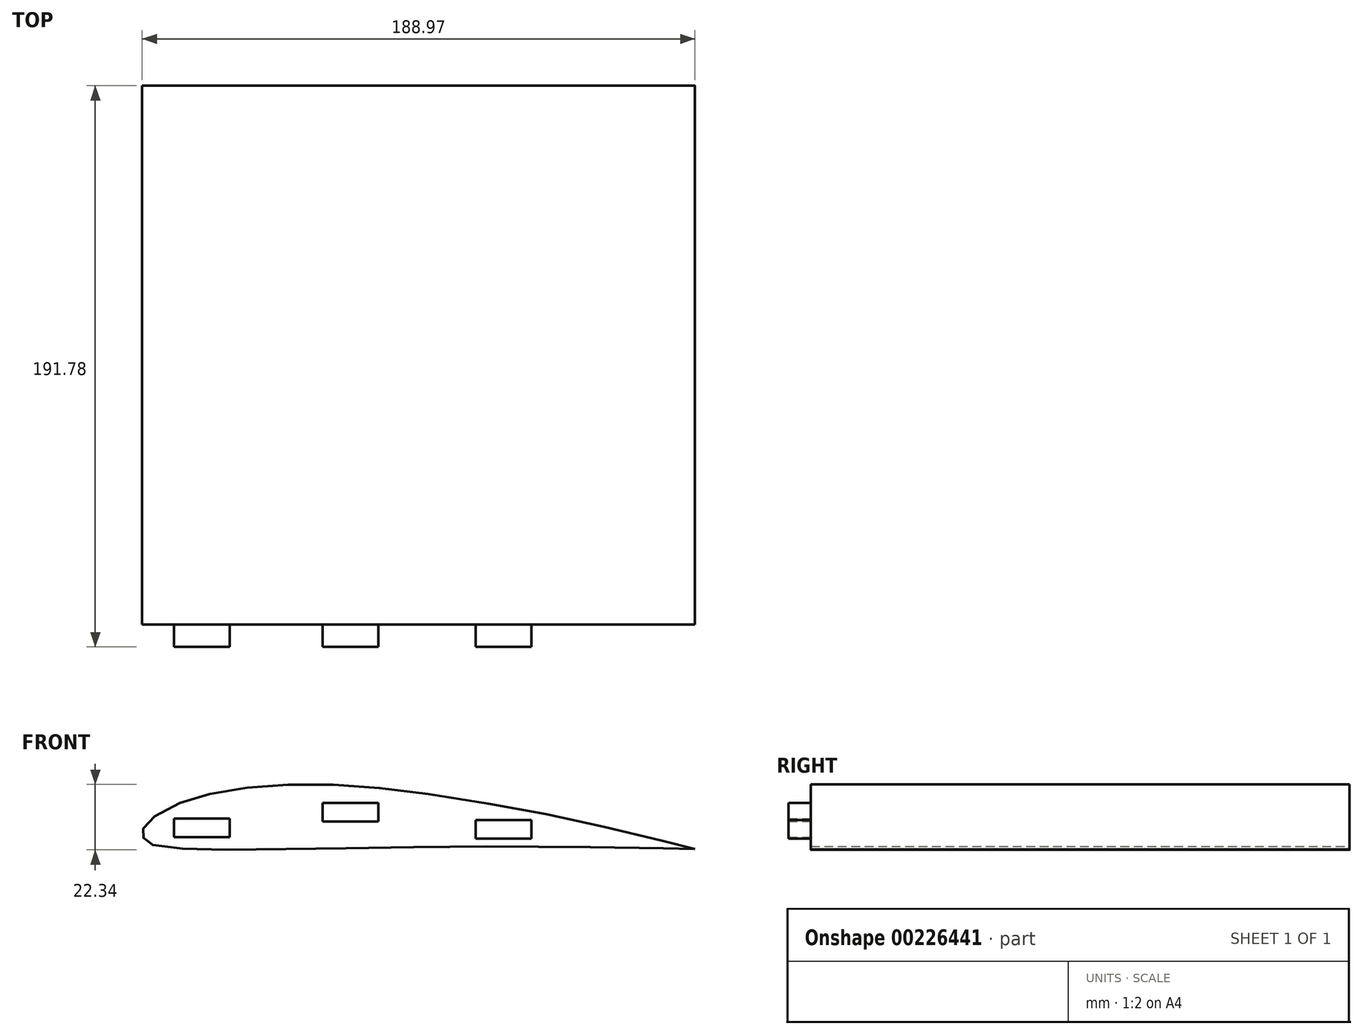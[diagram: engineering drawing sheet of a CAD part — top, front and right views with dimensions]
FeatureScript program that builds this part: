
annotation { "Feature Type Name" : "Feature", "Feature Type Description" : "" }
export const myFeature = defineFeature(function(context is Context, id is Id, definition is map)
    precondition{}
    {
        {
            var Q0;
            Q0=qCreatedBy(makeId("Front.planeOp"),FACE);
            var sketch = newSketch(context, id + "F0", { "sketchPlane" : qUnion([Q0])});
            skFitSpline(sketch, "E0.0", {"points": [v(330.51, -26.8) * mm, v(330.41, -27.02) * mm, v(320.9, -26.65) * mm, v(282.9, -25.74) * mm, v(133.46, -23.45) * mm, v(-1.4, -24.3) * mm, v(-5.52, -24.35) * mm, v(-223.27, -27.63) * mm, v(-263.84, -26.15) * mm, v(-289.63, -25.37) * mm, v(-306.1, -22.64) * mm, v(-310.34, -21.37) * mm, v(-312.97, -20.17) * mm, v(-315.36, -18.5) * mm, v(-317.44, -16.46) * mm, v(-318.92, -14.43) * mm, v(-319.94, -12.57) * mm, v(-320.57, -10.76) * mm, v(-320.82, -9.61) * mm, v(-320.99, -7.97) * mm, v(-320.86, -6.28) * mm, v(-320.4, -4.3) * mm, v(-319.53, -2.04) * mm, v(-317.5, 1.34) * mm, v(-314.64, 4.78) * mm, v(-309.38, 9.62) * mm, v(-300.92, 15.27) * mm, v(-284.86, 23.88) * mm, v(-268.85, 30.71) * mm, v(-251.3, 35.74) * mm, v(-225.1, 41.46) * mm, v(-196.52, 45.77) * mm, v(-164.68, 48.46) * mm, v(-128.36, 49.34) * mm, v(-84.95, 48.6) * mm, v(-42.8, 45.45) * mm, v(0.59, 40.3) * mm, v(69.38, 29.76) * mm, v(139.47, 17.63) * mm, v(201.78, 4.38) * mm, v(277.63, -13.26) * mm, v(320.71, -24.55) * mm, v(330.61, -26.58) * mm, v(330.51, -26.8) * mm]});
            skPoint(sketch, "E1", {"position": v(330.51, -26.8) * mm});
            skPoint(sketch, "E2", {"position": v(-320.85, -9.19) * mm});
            skSolve(sketch);
        }
        {
            var Q0;
            Q0=makeQuery(id+"F0.imprint","IMPRINT",FACE,{"disambiguationData":[TD([[makeQuery(id+"F0.imprint","IMPRINT",EDGE,{"derivedFrom":sQuery(id+"F0.wireOp",EDGE,"E0.0")}),-1.0]])]});
            extrude(context, id + "F1", {"entities" : qUnion([Q0]), "depth" : 635 * mm, "symmetric" : true});
        }
        {
            var Q0;
            Q0=makeQuery(id+"F1.opExtrude","SWEPT_BODY",BODY,{"disambiguationData":[OSD([sQuery(id+"F0.wireOp",EDGE,"E0.0")])]});
            var Q1;
            Q1=qCreatedBy(makeId("Origin.pointOp"),VERTEX);
            transform(context, id + "F2", {"entities" : qUnion([Q0]), "transformType" : TransformType.SCALE_UNIFORMLY, "scale" : .29, "scalePoint" : qUnion([Q1]), "makeCopy" : false});
        }
        {
            var Q0;
            Q0=makeQuery(id+"F1.opExtrude","CAP_FACE",FACE,{"disambiguationData":[OSD([sQuery(id+"F0.wireOp",EDGE,"E0.0")])],"isStart":false});
            var sketch = newSketch(context, id + "F3", { "sketchPlane" : qUnion([Q0])});
            skFitSpline(sketch, "E3.0", {"points": [v(95.85, -7.77) * mm, v(95.82, -7.84) * mm, v(93.06, -7.73) * mm, v(82.04, -7.47) * mm, v(38.7, -6.8) * mm, v(-0.4, -7.05) * mm, v(-1.6, -7.06) * mm, v(-64.75, -8.01) * mm, v(-76.51, -7.58) * mm, v(-84, -7.36) * mm, v(-88.77, -6.57) * mm, v(-90, -6.2) * mm, v(-90.76, -5.85) * mm, v(-91.45, -5.37) * mm, v(-92.06, -4.77) * mm, v(-92.49, -4.19) * mm, v(-92.78, -3.65) * mm, v(-92.96, -3.12) * mm, v(-93.04, -2.79) * mm, v(-93.09, -2.31) * mm, v(-93.05, -1.82) * mm, v(-92.92, -1.25) * mm, v(-92.66, -0.6) * mm, v(-92.08, 0.39) * mm, v(-91.24, 1.39) * mm, v(-89.72, 2.79) * mm, v(-87.27, 4.43) * mm, v(-82.61, 6.93) * mm, v(-77.97, 8.9) * mm, v(-72.88, 10.37) * mm, v(-65.28, 12.02) * mm, v(-57, 13.27) * mm, v(-47.76, 14.05) * mm, v(-37.23, 14.3) * mm, v(-24.64, 14.1) * mm, v(-12.41, 13.18) * mm, v(0.17, 11.69) * mm, v(20.12, 8.63) * mm, v(40.45, 5.11) * mm, v(58.52, 1.27) * mm, v(80.51, -3.84) * mm, v(93, -7.12) * mm, v(95.88, -7.7) * mm, v(95.85, -7.77) * mm]});
            skPoint(sketch, "E4", {"position": v(-93.07, -2.2) * mm});
            skPoint(sketch, "E5", {"position": v(95.64, -7.8) * mm});
            skLineSegment(sketch, "E6.bottom", {"start": v(-63.23, -3.61) * mm, "end": v(-82.28, -3.61) * mm});
            skLineSegment(sketch, "E6.top", {"start": v(-63.23, 2.74) * mm, "end": v(-82.28, 2.74) * mm});
            skLineSegment(sketch, "E6.left", {"start": v(-63.23, -3.61) * mm, "end": v(-63.23, 2.74) * mm});
            skLineSegment(sketch, "E6.right", {"start": v(-82.28, -3.61) * mm, "end": v(-82.28, 2.74) * mm});
            skPoint(sketch, "E6.middle", {"position": v(-72.75, -0.44) * mm});
            skLineSegment(sketch, "E7.bottom", {"start": v(-12.43, 1.72) * mm, "end": v(-31.48, 1.72) * mm});
            skLineSegment(sketch, "E7.top", {"start": v(-12.43, 8.07) * mm, "end": v(-31.48, 8.07) * mm});
            skLineSegment(sketch, "E7.left", {"start": v(-12.43, 1.72) * mm, "end": v(-12.43, 8.07) * mm});
            skLineSegment(sketch, "E7.right", {"start": v(-31.48, 1.72) * mm, "end": v(-31.48, 8.07) * mm});
            skPoint(sketch, "E7.middle", {"position": v(-21.95, 4.9) * mm});
            skLineSegment(sketch, "E8.bottom", {"start": v(40, -4.2) * mm, "end": v(20.95, -4.2) * mm});
            skLineSegment(sketch, "E8.top", {"start": v(40, 2.16) * mm, "end": v(20.95, 2.16) * mm});
            skLineSegment(sketch, "E8.left", {"start": v(40, -4.2) * mm, "end": v(40, 2.16) * mm});
            skLineSegment(sketch, "E8.right", {"start": v(20.95, -4.2) * mm, "end": v(20.95, 2.16) * mm});
            skPoint(sketch, "E8.middle", {"position": v(30.48, -1.02) * mm});
            skLineSegment(sketch, "E9", {"start": v(95.64, -7.8) * mm, "end": v(-115.1, -7.8) * mm, "construction": true});
            skSolve(sketch);
        }
        {
            var Q0;
            Q0=makeQuery(id+"F3.imprint","IMPRINT",FACE,{"disambiguationData":[TD([[makeQuery(id+"F3.imprint","IMPRINT",EDGE,{"derivedFrom":sQuery(id+"F3.wireOp",EDGE,"E6.bottom")}),-1.0]])]});
            var Q1;
            Q1=makeQuery(id+"F3.imprint","IMPRINT",FACE,{"disambiguationData":[TD([[makeQuery(id+"F3.imprint","IMPRINT",EDGE,{"derivedFrom":sQuery(id+"F3.wireOp",EDGE,"E7.bottom")}),-1.0]])]});
            var Q2;
            Q2=makeQuery(id+"F3.imprint","IMPRINT",FACE,{"disambiguationData":[TD([[makeQuery(id+"F3.imprint","IMPRINT",EDGE,{"derivedFrom":sQuery(id+"F3.wireOp",EDGE,"E8.bottom")}),-1.0]])]});
            extrude(context, id + "F4", {"entities" : qUnion([Q0, Q1, Q2]), "operationType" : NewBodyOperationType.ADD, "depth" : 7.62 * mm});
        }
    });
